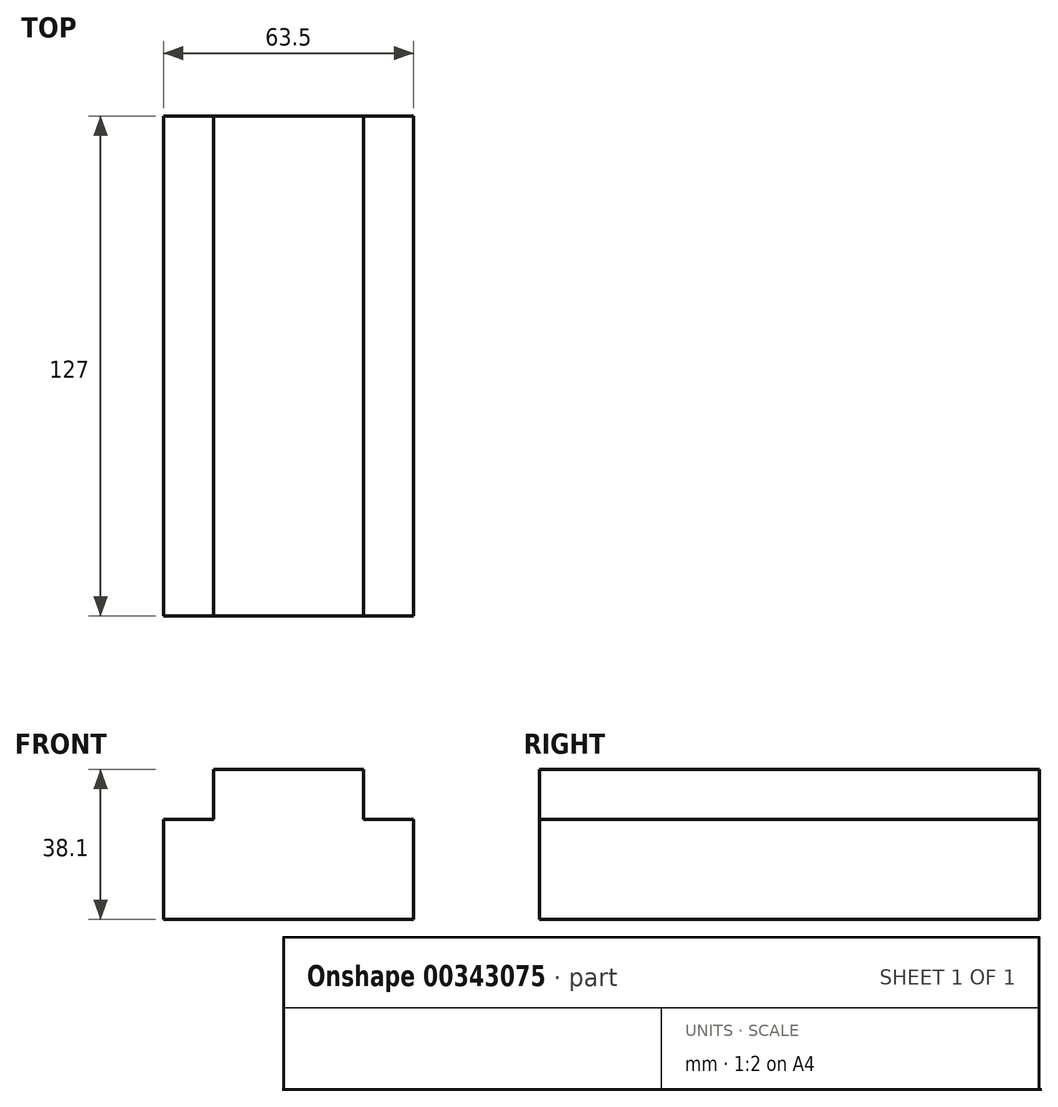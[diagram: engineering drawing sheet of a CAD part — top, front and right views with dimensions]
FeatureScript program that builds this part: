
annotation { "Feature Type Name" : "Feature", "Feature Type Description" : "" }
export const myFeature = defineFeature(function(context is Context, id is Id, definition is map)
    precondition{}
    {
        {
            var Q0;
            Q0=qCreatedBy(makeId("Front.planeOp"),FACE);
            var sketch = newSketch(context, id + "F0", { "sketchPlane" : qUnion([Q0])});
            skLineSegment(sketch, "E0", {"start": v(30.27, -49.11) * mm, "end": v(30.27, -23.71) * mm});
            skLineSegment(sketch, "E1", {"start": v(30.27, -23.71) * mm, "end": v(17.57, -23.71) * mm});
            skLineSegment(sketch, "E2", {"start": v(17.57, -23.71) * mm, "end": v(17.57, -11.01) * mm});
            skLineSegment(sketch, "E3", {"start": v(30.27, -49.11) * mm, "end": v(-33.23, -49.11) * mm});
            skLineSegment(sketch, "E4", {"start": v(-33.23, -49.11) * mm, "end": v(-33.23, -23.71) * mm});
            skLineSegment(sketch, "E5", {"start": v(-33.23, -23.71) * mm, "end": v(-20.53, -23.71) * mm});
            skLineSegment(sketch, "E6", {"start": v(-20.53, -23.71) * mm, "end": v(-20.53, -11.01) * mm});
            skLineSegment(sketch, "E7", {"start": v(-20.53, -11.01) * mm, "end": v(17.57, -11.01) * mm});
            skSolve(sketch);
        }
        {
            var Q0;
            Q0 = qSketchRegion(id + "F0", true);
            extrude(context, id + "F1", {"entities" : qUnion([Q0]), "depth" : 127 * mm});
        }
    });
